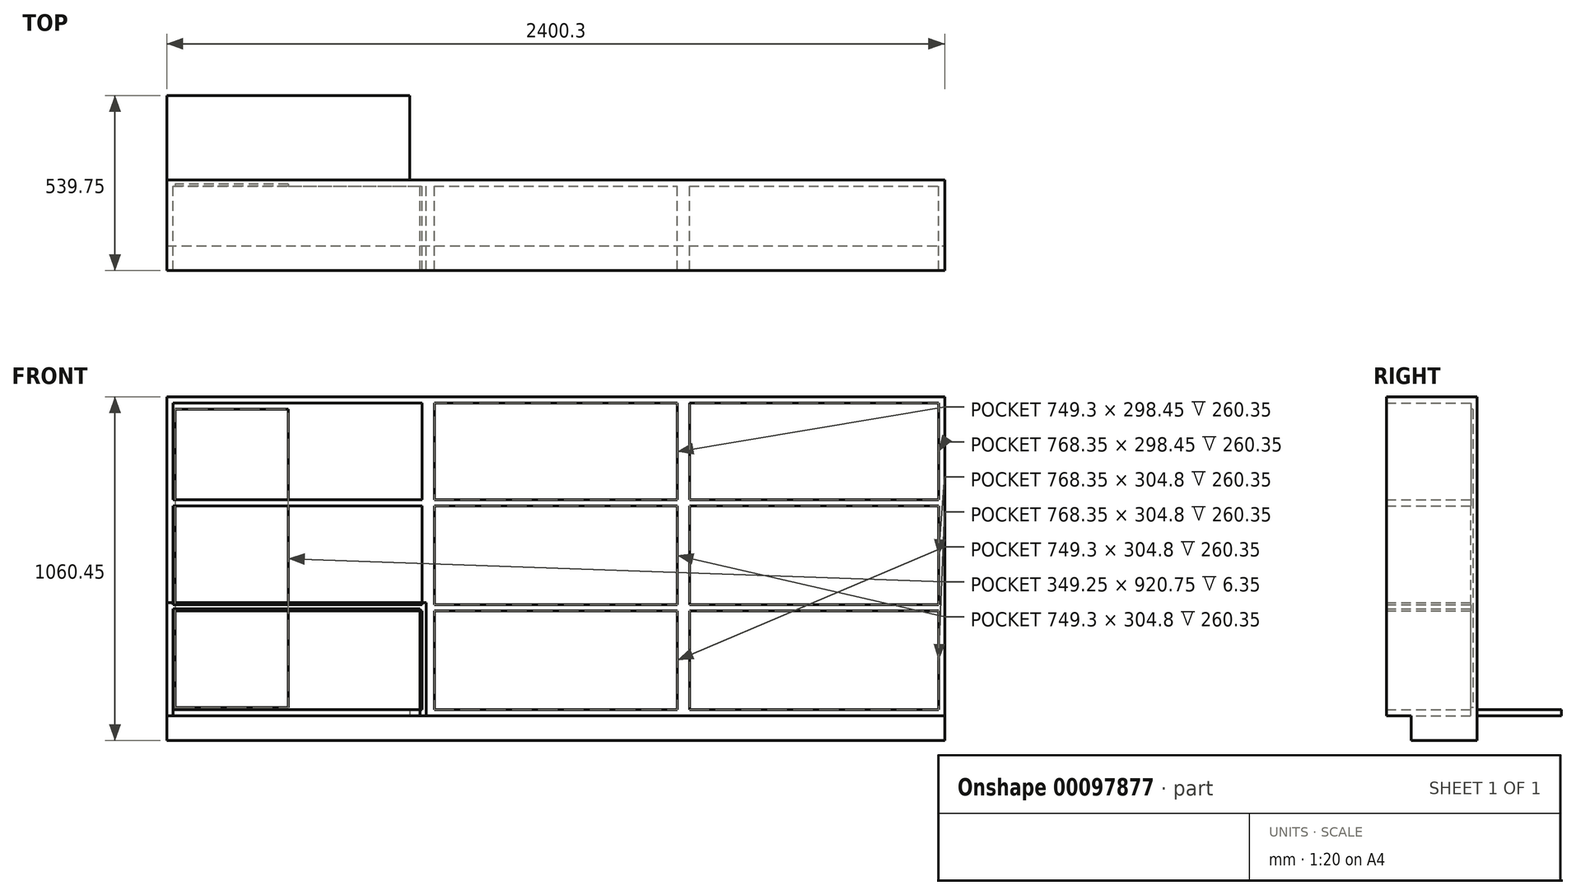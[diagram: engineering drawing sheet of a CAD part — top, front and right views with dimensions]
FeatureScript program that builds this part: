
annotation { "Feature Type Name" : "Feature", "Feature Type Description" : "" }
export const myFeature = defineFeature(function(context is Context, id is Id, definition is map)
    precondition{}
    {
        {
            var Q0;
            Q0=qCreatedBy(makeId("Front.planeOp"),FACE);
            var sketch = newSketch(context, id + "F0", { "sketchPlane" : qUnion([Q0])});
            skLineSegment(sketch, "E0.bottom", {"start": v(0, 0) * mm, "end": v(2400.3, 0) * mm});
            skLineSegment(sketch, "E0.left", {"start": v(0, 0) * mm, "end": v(0, 984.25) * mm});
            skLineSegment(sketch, "E0.right", {"start": v(2400.3, 0) * mm, "end": v(2400.3, 984.25) * mm});
            skLineSegment(sketch, "E1", {"start": v(0, 984.25) * mm, "end": v(800.1, 984.25) * mm, "construction": true});
            skLineSegment(sketch, "E2", {"start": v(800.1, 984.25) * mm, "end": v(1600.2, 984.25) * mm, "construction": true});
            skLineSegment(sketch, "E3", {"start": v(1600.2, 984.25) * mm, "end": v(2400.3, 984.25) * mm, "construction": true});
            skLineSegment(sketch, "E4", {"start": v(0, 984.25) * mm, "end": v(2400.3, 984.25) * mm});
            skLineSegment(sketch, "E5", {"start": v(800.1, 984.25) * mm, "end": v(800.1, 0) * mm, "construction": true});
            skLineSegment(sketch, "E6", {"start": v(1600.2, 984.25) * mm, "end": v(1600.2, 0) * mm, "construction": true});
            skSolve(sketch);
        }
        {
            var Q0;
            Q0 = qSketchRegion(id + "F0", true);
            extrude(context, id + "F1", {"entities" : qUnion([Q0]), "depth" : 279.4 * mm});
        }
        {
            var Q0;
            Q0=makeQuery(id+"F1.opExtrude","CAP_FACE",FACE,{"disambiguationData":[OSD([sQuery(id+"F0.wireOp",EDGE,"E0.bottom"),sQuery(id+"F0.wireOp",EDGE,"E0.left"),sQuery(id+"F0.wireOp",EDGE,"E0.right"),sQuery(id+"F0.wireOp",EDGE,"E4")])],"isStart":false});
            shell(context, id + "F2", {"entities" : qUnion([Q0]), "thickness" : 19.05 * mm});
        }
        {
            var Q0;
            Q0=makeQuery(id+"F1.opExtrude","SWEPT_FACE",FACE,{"disambiguationData":[OSD([sQuery(id+"F0.wireOp",EDGE,"E0.bottom")])]});
            var sketch = newSketch(context, id + "F3", { "sketchPlane" : qUnion([Q0])});
            skLineSegment(sketch, "E7.bottom", {"start": v(0, 0) * mm, "end": v(2400.3, 0) * mm});
            skLineSegment(sketch, "E7.top", {"start": v(0, 203.2) * mm, "end": v(2400.3, 203.2) * mm});
            skLineSegment(sketch, "E7.left", {"start": v(0, 0) * mm, "end": v(0, 203.2) * mm});
            skLineSegment(sketch, "E7.right", {"start": v(2400.3, 0) * mm, "end": v(2400.3, 203.2) * mm});
            skSolve(sketch);
        }
        {
            var Q0;
            Q0 = qSketchRegion(id + "F3", true);
            extrude(context, id + "F4", {"entities" : qUnion([Q0]), "operationType" : NewBodyOperationType.ADD, "depth" : 76.2 * mm});
        }
        {
            var Q0;
            Q0=qCreatedBy(makeId("Front.planeOp"),FACE);
            var sketch = newSketch(context, id + "F5", { "sketchPlane" : qUnion([Q0])});
            skLineSegment(sketch, "E8.bottom", {"start": v(0, 0) * mm, "end": v(400.05, 0) * mm});
            skLineSegment(sketch, "E8.top", {"start": v(0, 971.55) * mm, "end": v(400.05, 971.55) * mm});
            skLineSegment(sketch, "E8.left", {"start": v(0, 0) * mm, "end": v(0, 971.55) * mm});
            skLineSegment(sketch, "E8.right", {"start": v(400.05, 0) * mm, "end": v(400.05, 971.55) * mm});
            skSolve(sketch);
        }
        {
            var Q0;
            Q0=makeQuery(id+"F5.imprint","IMPRINT",FACE,{"disambiguationData":[TD([[makeQuery(id+"F5.imprint","IMPRINT",EDGE,{"derivedFrom":sQuery(id+"F5.wireOp",EDGE,"E8.bottom")}),1.0]])]});
            extrude(context, id + "F6", {"entities" : qUnion([Q0]), "depth" : 19.05 * mm});
        }
        {
            var Q0;
            Q0=makeQuery(id+"F6.opExtrude","CAP_FACE",FACE,{"disambiguationData":[OSD([sQuery(id+"F5.wireOp",EDGE,"E8.bottom"),sQuery(id+"F5.wireOp",EDGE,"E8.top"),sQuery(id+"F5.wireOp",EDGE,"E8.left"),sQuery(id+"F5.wireOp",EDGE,"E8.right")])],"isStart":false});
            var sketch = newSketch(context, id + "F7", { "sketchPlane" : qUnion([Q0])});
            skLineSegment(sketch, "E9.0", {"start": v(25.4, 946.15) * mm, "end": v(25.4, 25.4) * mm});
            skLineSegment(sketch, "E9.1", {"start": v(374.65, 946.15) * mm, "end": v(25.4, 946.15) * mm});
            skLineSegment(sketch, "E9.2", {"start": v(374.65, 25.4) * mm, "end": v(374.65, 946.15) * mm});
            skLineSegment(sketch, "E9.3", {"start": v(25.4, 25.4) * mm, "end": v(374.65, 25.4) * mm});
            skSolve(sketch);
        }
        {
            var Q0;
            Q0 = qSketchRegion(id + "F7", true);
            extrude(context, id + "F8", {"entities" : qUnion([Q0]), "operationType" : NewBodyOperationType.REMOVE, "oppositeDirection" : true, "depth" : 6.35 * mm});
        }
        {
            var Q0;
            Q0=makeQuery(id+"F2.opShell","OFFSET_FACE",FACE,{"disambiguationData":[OSD([sQuery(id+"F0.wireOp",EDGE,"E0.bottom"),sQuery(id+"F0.wireOp",EDGE,"E0.left"),sQuery(id+"F0.wireOp",EDGE,"E0.right"),sQuery(id+"F0.wireOp",EDGE,"E4")])]});
            var sketch = newSketch(context, id + "F9", { "sketchPlane" : qUnion([Q0])});
            skLineSegment(sketch, "E10.bottom", {"start": v(787.4, 965.2) * mm, "end": v(825.5, 965.2) * mm});
            skLineSegment(sketch, "E10.top", {"start": v(787.4, 19.05) * mm, "end": v(825.5, 19.05) * mm});
            skLineSegment(sketch, "E10.left", {"start": v(787.4, 965.2) * mm, "end": v(787.4, 19.05) * mm});
            skLineSegment(sketch, "E10.right", {"start": v(825.5, 965.2) * mm, "end": v(825.5, 19.05) * mm});
            skPoint(sketch, "E11", {"position": v(806.45, 965.2) * mm});
            skLineSegment(sketch, "E12", {"start": v(1200.15, 965.2) * mm, "end": v(1200.15, 19.05) * mm, "construction": true});
            skLineSegment(sketch, "E13.MirrorCS", {"start": v(1612.9, 965.2) * mm, "end": v(1574.8, 965.2) * mm});
            skLineSegment(sketch, "E14.MirrorCS", {"start": v(1612.9, 19.05) * mm, "end": v(1574.8, 19.05) * mm});
            skPoint(sketch, "E15.MirrorP", {"position": v(1593.85, 965.2) * mm});
            skLineSegment(sketch, "E16.MirrorCS", {"start": v(1612.9, 965.2) * mm, "end": v(1612.9, 19.05) * mm});
            skLineSegment(sketch, "E17.MirrorCS", {"start": v(1574.8, 965.2) * mm, "end": v(1574.8, 19.05) * mm});
            skLineSegment(sketch, "E18.bottom", {"start": v(19.05, 666.75) * mm, "end": v(2381.25, 666.75) * mm});
            skLineSegment(sketch, "E18.top", {"start": v(19.05, 647.7) * mm, "end": v(2381.25, 647.7) * mm});
            skLineSegment(sketch, "E18.left", {"start": v(19.05, 666.75) * mm, "end": v(19.05, 647.7) * mm});
            skLineSegment(sketch, "E18.right", {"start": v(2381.25, 666.75) * mm, "end": v(2381.25, 647.7) * mm});
            skLineSegment(sketch, "E19.bottom", {"start": v(19.05, 342.9) * mm, "end": v(2381.25, 342.9) * mm});
            skLineSegment(sketch, "E19.top", {"start": v(19.05, 323.85) * mm, "end": v(2381.25, 323.85) * mm});
            skLineSegment(sketch, "E19.left", {"start": v(19.05, 342.9) * mm, "end": v(19.05, 323.85) * mm});
            skLineSegment(sketch, "E19.right", {"start": v(2381.25, 342.9) * mm, "end": v(2381.25, 323.85) * mm});
            skSolve(sketch);
        }
        {
            var Q0;
            Q0 = qSketchRegion(id + "F9", true);
            var Q1;
            Q1=makeQuery(id+"F1.opExtrude","CAP_FACE",FACE,{"disambiguationData":[OSD([sQuery(id+"F0.wireOp",EDGE,"E0.bottom"),sQuery(id+"F0.wireOp",EDGE,"E0.left"),sQuery(id+"F0.wireOp",EDGE,"E0.right"),sQuery(id+"F0.wireOp",EDGE,"E4")])],"isStart":false});
            extrude(context, id + "F10", {"entities" : qUnion([Q0]), "operationType" : NewBodyOperationType.ADD, "endBound" : BoundingType.UP_TO_SURFACE, "endBoundEntityFace" : qUnion([Q1]), "depth" : 25.4 * mm});
        }
        {
            var Q0;
            Q0=qCreatedBy(makeId("Top.planeOp"),FACE);
            var sketch = newSketch(context, id + "F11", { "sketchPlane" : qUnion([Q0])});
            skLineSegment(sketch, "E20.bottom", {"start": v(0, 0) * mm, "end": v(749.3, 0) * mm});
            skLineSegment(sketch, "E20.top", {"start": v(0, 260.35) * mm, "end": v(749.3, 260.35) * mm});
            skLineSegment(sketch, "E20.left", {"start": v(0, 0) * mm, "end": v(0, 260.35) * mm});
            skLineSegment(sketch, "E20.right", {"start": v(749.3, 0) * mm, "end": v(749.3, 260.35) * mm});
            skSolve(sketch);
        }
        {
            var Q0;
            Q0=makeQuery(id+"F11.imprint","IMPRINT",FACE,{"disambiguationData":[TD([[makeQuery(id+"F11.imprint","IMPRINT",EDGE,{"derivedFrom":sQuery(id+"F11.wireOp",EDGE,"E20.bottom")}),1.0]])]});
            extrude(context, id + "F12", {"entities" : qUnion([Q0]), "depth" : 19.05 * mm});
        }
        {
            var Q0;
            Q0=qCreatedBy(makeId("Front.planeOp"),FACE);
            var sketch = newSketch(context, id + "F13", { "sketchPlane" : qUnion([Q0])});
            skLineSegment(sketch, "E21.bottom", {"start": v(0, 0) * mm, "end": v(800.1, 0) * mm});
            skLineSegment(sketch, "E21.top", {"start": v(0, 349.25) * mm, "end": v(800.1, 349.25) * mm});
            skLineSegment(sketch, "E21.left", {"start": v(0, 0) * mm, "end": v(0, 349.25) * mm});
            skLineSegment(sketch, "E21.right", {"start": v(800.1, 0) * mm, "end": v(800.1, 349.25) * mm});
            skSolve(sketch);
        }
        {
            var Q0;
            Q0=makeQuery(id+"F13.imprint","IMPRINT",FACE,{"disambiguationData":[TD([[makeQuery(id+"F13.imprint","IMPRINT",EDGE,{"derivedFrom":sQuery(id+"F13.wireOp",EDGE,"E21.bottom")}),1.0]])]});
            extrude(context, id + "F14", {"entities" : qUnion([Q0]), "depth" : 279.4 * mm});
        }
        {
            var Q0;
            Q0=makeQuery(id+"F14.opExtrude","CAP_FACE",FACE,{"disambiguationData":[OSD([sQuery(id+"F13.wireOp",EDGE,"E21.bottom"),sQuery(id+"F13.wireOp",EDGE,"E21.top"),sQuery(id+"F13.wireOp",EDGE,"E21.left"),sQuery(id+"F13.wireOp",EDGE,"E21.right")])],"isStart":false});
            var Q1;
            Q1=makeQuery(id+"F14.opExtrude","SWEPT_FACE",FACE,{"disambiguationData":[OSD([sQuery(id+"F13.wireOp",EDGE,"E21.bottom")])]});
            shell(context, id + "F15", {"entities" : qUnion([Q0, Q1]), "thickness" : 19.05 * mm});
        }
    });
